# Revit family: 145-56-001-DN65-200
name_source: partatom
category: Pipe Accessories
units: mm (PartAtom-declared; Revit-internal decimal feet)

## family parameters
Always vertical = No
Cut with Voids When Loaded = No
Part Type = Valve - Breaks Into
Round Connector Dimension = Use Diameter
Shared = No
Work Plane-Based = No

## types (5) — shared parameters
Body_Wallthickness = 15 mm  [stored 0.0492126 ft]
DN 065 = Yes
DN 080 = Yes
DN 100 = Yes
DN 150 = Yes
DN 200 = Yes
DN065_PN10/16 = 145-065-56-01366120
DN080_PN10/16 = 145-080-56-01366120
DN100_PN10/16 = 145-100-56-01366120
DN150_PN10/16 = 145-150-56-01366120
DN200_PN10 = 145-200-56-00366120
DN200_PN16 = 145-200-56-01366120
Description_ = AVK GATE VALVE, FLANGED, OS&Y, UL/FM APPROVED
Ftc = 4 mm  [stored 0.0131234 ft]
Name_Height_reference = 10 mm  [stored 0.0328084 ft]
Rib_Height_Reference_1 = 120 mm
Rib_Height_Reference_2 = 110 mm
Rib_Height_Reference_3 = 100 mm
Rib_Thickness = 18 mm  [stored 0.0590551 ft]
Search_table = 145-56-001-DN65-200
URL product pages = https://www.avkvalves.com
zero-valued in all types: Bottom_Reference

## per-type parameters (varying)
- DN 065: At=53.5 mm; Body_Height=95 mm; Body_depth=107 mm; Body_width=60 mm; Bonnet_Flange_Depth=135 mm; Bonnet_Flange_Width=65 mm; Bonnet_Flange_cut=7.5 mm  [stored 0.0246063 ft]; Bonnet_Flange_thickness=15 mm  [stored 0.0492126 ft]; Bonnet_H=138 mm; Bonnet_H_Ref=153.5 mm; Bonnet_Height=44.5 mm  [stored 0.145997 ft]; Bonnet_Reference_height=85 mm; Bonnet_Thickness=61.2 mm; Bonnet_W=60 mm; Bt=61.2 mm; Bt_2=54 mm; CL _Thickness=19 mm  [stored 0.062336 ft]; CL_Height=58.5 mm; CL_Height_2=19.5 mm  [stored 0.0639764 ft]; Cut_Reference=380 mm; D=82.5 mm; D1=10 mm  [stored 0.0328084 ft]; F1=20 mm  [stored 0.0656168 ft]; Fillet_Thickness=6 mm  [stored 0.019685 ft]; Flange_OR=89 mm; Flange_Thickness=19 mm  [stored 0.062336 ft]; Flange_Thickness_cut=28.25 mm  [stored 0.0926837 ft]; Ftc_reference_height=89 mm; HW_Dia=15 mm  [stored 0.0492126 ft]; HW_H_ref=7.5 mm  [stored 0.0246063 ft]; HW_Rib_depth=152 mm; HW_Rib_width=15 mm  [stored 0.0492126 ft]; Hc=326 mm; Ho=401 mm; Horizontal_Flange_width=186 mm; ID (Radius)=32.5 mm  [stored 0.106627 ft]; L=190 mm; L_Dia=65 mm; Name_Reference=96 mm; Name_Width=30 mm  [stored 0.0984252 ft]; Neck_T=17 mm  [stored 0.0557743 ft]; Nominal Diameter (DN)=65 mm; R1tv=890 mm; R2f=15 mm  [stored 0.0492126 ft]; RF_Dia=59 mm; Rf=310 mm; Rib_Height_Reference_4=75 mm; Rib_Width_1=30 mm  [stored 0.0984252 ft]; Rib_Width_2=30 mm  [stored 0.0984252 ft]; Rib_Width_3=30 mm  [stored 0.0984252 ft]; Rib_depth_1=30 mm  [stored 0.0984252 ft]; Rib_depth_2=30 mm  [stored 0.0984252 ft]; Rib_depth_3=30 mm  [stored 0.0984252 ft]; Rt=296.67 mm; W=178 mm
- DN 080: At=54.5 mm; Body_Height=120 mm; Body_depth=109 mm; Body_width=75 mm; Bonnet_Flange_Depth=160 mm; Bonnet_Flange_Width=96 mm; Bonnet_Flange_cut=7.5 mm  [stored 0.0246063 ft]; Bonnet_Flange_thickness=15 mm  [stored 0.0492126 ft]; Bonnet_H=155.67 mm; Bonnet_H_Ref=179.5 mm; Bonnet_Height=47.75 mm; Bonnet_Reference_height=110 mm; Bonnet_Thickness=76.5 mm; Bonnet_W=70 mm; Bt=76.5 mm; Bt_2=69 mm; CL _Thickness=26.5 mm  [stored 0.0869423 ft]; CL_Height=59.5 mm; CL_Height_2=19.83 mm; Cut_Reference=406 mm; D=82.5 mm; D1=10 mm  [stored 0.0328084 ft]; F1=20 mm  [stored 0.0656168 ft]; Fillet_Thickness=6 mm  [stored 0.019685 ft]; Flange_OR=95.5 mm; Flange_Thickness=19 mm  [stored 0.062336 ft]; Flange_Thickness_cut=27.75 mm  [stored 0.0910433 ft]; Ftc_reference_height=95.5 mm; HW_Dia=15 mm  [stored 0.0492126 ft]; HW_H_ref=7.5 mm  [stored 0.0246063 ft]; HW_Rib_depth=152 mm; HW_Rib_width=15 mm  [stored 0.0492126 ft]; Hc=370 mm; Ho=453 mm; Horizontal_Flange_width=200 mm; ID (Radius)=40 mm  [stored 0.131234 ft]; L=203 mm; L_Dia=80 mm; Name_Reference=90 mm; Name_Width=37.5 mm; Neck_T=24.5 mm; Nominal Diameter (DN)=80 mm; R1tv=955 mm; R2f=15 mm  [stored 0.0492126 ft]; RF_Dia=66.9 mm; Rf=333.33 mm; Rib_Height_Reference_4=85 mm; Rib_Width_1=37.5 mm; Rib_Width_2=37.5 mm; Rib_Width_3=37.5 mm; Rib_depth_1=37.5 mm; Rib_depth_2=37.5 mm; Rib_depth_3=37.5 mm; Rt=318.33 mm; W=191 mm
- DN 100: At=76.5 mm; Body_Height=122 mm; Body_depth=153 mm; Body_width=80 mm; Bonnet_Flange_Depth=180 mm; Bonnet_Flange_Width=81 mm; Bonnet_Flange_cut=7.5 mm  [stored 0.0246063 ft]; Bonnet_Flange_thickness=15 mm  [stored 0.0492126 ft]; Bonnet_H=204.33 mm; Bonnet_H_Ref=203.5 mm; Bonnet_Height=57.25 mm; Bonnet_Reference_height=112 mm; Bonnet_Thickness=81.6 mm; Bonnet_W=80 mm; Bt=81.6 mm; Bt_2=74 mm; CL _Thickness=29 mm  [stored 0.0951444 ft]; CL_Height=81.5 mm; CL_Height_2=27.17 mm; Cut_Reference=458 mm; D=119.5 mm; D1=12.5 mm  [stored 0.0410105 ft]; F1=22 mm  [stored 0.0721785 ft]; Fillet_Thickness=6 mm  [stored 0.019685 ft]; Flange_OR=114.5 mm; Flange_Thickness=19 mm  [stored 0.062336 ft]; Flange_Thickness_cut=32.25 mm; Ftc_reference_height=114.5 mm; HW_Dia=15 mm  [stored 0.0492126 ft]; HW_H_ref=7.5 mm  [stored 0.0246063 ft]; HW_Rib_depth=226 mm; HW_Rib_width=15 mm  [stored 0.0492126 ft]; Hc=450 mm; Ho=559 mm; Horizontal_Flange_width=220 mm; ID (Radius)=50 mm; L=229 mm; L_Dia=100 mm; Name_Reference=101 mm; Name_Width=40 mm  [stored 0.131234 ft]; Neck_T=27 mm; Nominal Diameter (DN)=100 mm; R1tv=1145 mm; R2f=15 mm  [stored 0.0492126 ft]; RF_Dia=76.5 mm; Rf=366.67 mm; Rib_Height_Reference_4=90 mm; Rib_Width_1=40 mm  [stored 0.131234 ft]; Rib_Width_2=40 mm  [stored 0.131234 ft]; Rib_Width_3=40 mm  [stored 0.131234 ft]; Rib_depth_1=40 mm  [stored 0.131234 ft]; Rib_depth_2=40 mm  [stored 0.131234 ft]; Rib_depth_3=40 mm  [stored 0.131234 ft]; Rt=381.67 mm; W=229 mm
- DN 150: At=109 mm; Body_Height=173 mm; Body_depth=218 mm; Body_width=95 mm; Bonnet_Flange_Depth=270 mm; Bonnet_Flange_Width=154 mm; Bonnet_Flange_cut=7.5 mm  [stored 0.0246063 ft]; Bonnet_Flange_thickness=15 mm  [stored 0.0492126 ft]; Bonnet_H=252 mm; Bonnet_H_Ref=287 mm; Bonnet_Height=69.75 mm; Bonnet_Reference_height=163 mm; Bonnet_Thickness=96.9 mm; Bonnet_W=90 mm; Bt=96.9 mm; Bt_2=89 mm; CL _Thickness=33.5 mm; CL_Height=114 mm; CL_Height_2=38 mm  [stored 0.124672 ft]; Cut_Reference=534 mm; D=145 mm; D1=14 mm  [stored 0.0459318 ft]; F1=22 mm  [stored 0.0721785 ft]; Fillet_Thickness=12 mm  [stored 0.0393701 ft]; Flange_OR=139.5 mm; Flange_Thickness=19 mm  [stored 0.062336 ft]; Flange_Thickness_cut=32.25 mm; Ftc_reference_height=139.5 mm; HW_Dia=15 mm  [stored 0.0492126 ft]; HW_H_ref=7.5 mm  [stored 0.0246063 ft]; HW_Rib_depth=277 mm; HW_Rib_width=15 mm  [stored 0.0492126 ft]; Hc=592 mm; Ho=748 mm; Horizontal_Flange_width=286 mm; ID (Radius)=75 mm; L=267 mm; L_Dia=150 mm; Name_Reference=143 mm; Name_Width=47.5 mm; Neck_T=31.5 mm  [stored 0.103346 ft]; Nominal Diameter (DN)=150 mm; R1tv=1395 mm; R2f=30 mm  [stored 0.0984252 ft]; RF_Dia=104.5 mm; Rf=476.67 mm; Rib_Height_Reference_4=100 mm; Rib_Width_1=120 mm; Rib_Width_2=47.5 mm; Rib_Width_3=47.5 mm; Rib_depth_1=280 mm; Rib_depth_2=47.5 mm; Rib_depth_3=47.5 mm; Rt=465 mm; W=279 mm
- DN 200: At=126 mm; Body_Height=220 mm; Body_depth=252 mm; Body_width=108 mm; Bonnet_Flange_Depth=270 mm; Bonnet_Flange_Width=154 mm; Bonnet_Flange_cut=12.5 mm  [stored 0.0410105 ft]; Bonnet_Flange_thickness=25 mm  [stored 0.082021 ft]; Bonnet_H=333.33 mm; Bonnet_H_Ref=351 mm; Bonnet_Height=88 mm; Bonnet_Reference_height=210 mm; Bonnet_Thickness=110.16 mm; Bonnet_W=100 mm; Bt=110.16 mm; Bt_2=102 mm; CL _Thickness=34 mm  [stored 0.111549 ft]; CL_Height=131 mm; CL_Height_2=43.67 mm; Cut_Reference=584 mm; D=168 mm; D1=16 mm  [stored 0.0524934 ft]; F1=28 mm  [stored 0.0918635 ft]; Fillet_Thickness=24 mm  [stored 0.0787402 ft]; Flange_OR=176 mm; Flange_Thickness=20 mm  [stored 0.0656168 ft]; Flange_Thickness_cut=38 mm  [stored 0.124672 ft]; Ftc_reference_height=176 mm; HW_Dia=20 mm  [stored 0.0656168 ft]; HW_H_ref=10 mm  [stored 0.0328084 ft]; HW_Rib_depth=318 mm; HW_Rib_width=20 mm  [stored 0.0656168 ft]; Hc=748 mm; Ho=958 mm; Horizontal_Flange_width=340 mm; ID (Radius)=100 mm; L=292 mm; L_Dia=200 mm; Name_Reference=150 mm; Name_Width=54 mm; Neck_T=32 mm  [stored 0.104987 ft]; Nominal Diameter (DN)=200 mm; R1tv=1760 mm; R2f=60 mm; RF_Dia=132 mm; Rf=566.67 mm; Rib_Height_Reference_4=180 mm; Rib_Width_1=120 mm; Rib_Width_2=120 mm; Rib_Width_3=54 mm; Rib_depth_1=280 mm; Rib_depth_2=280 mm; Rib_depth_3=54 mm; Rt=586.67 mm; W=352 mm

note: [stored X ft] marks values corroborated as IEEE doubles in the binary element streams (Revit-internal decimal feet)

## geometry (parser evidence)
native form markers: Extrusion x1, Sweep x4
no freeform markers — native parametric forms only
